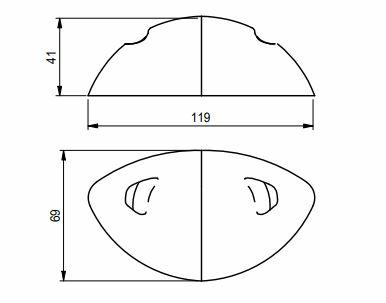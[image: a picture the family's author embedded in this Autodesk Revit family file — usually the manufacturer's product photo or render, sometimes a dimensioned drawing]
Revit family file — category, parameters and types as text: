
# Revit family: R-MBD-483
name_source: partatom
category: Portes
units: mm (PartAtom-declared; Revit-internal decimal feet)

## family parameters
Couper avec des vides une fois chargée = Non
Hôte = Mur
Partagée = Non
Repère de localisation dans la pièce = Oui
Toujours verticalement = Oui

## types (1)
- MBD-483
    1 Vantail = Oui
    2 Vantaux = Non
    A.E.V = non
    Acoustique = non
    Anti-Effraction = non
    Certification = D.A.S. Mode 2 certifié NF
    Code_MAJ = 2303130305MBD483
    Coloris_Chants = BER
    Coloris_Dormant = Hêtre
    Coloris_Face_Cote_Oppose_Ouverture = Prépeint
    Coloris_Face_Cote_Ouverture = Prépeint
    Construction analytique = <Aucun>
    DAS = Oui
    DC Larg Feuillure = 12 mm  [stored 0.0393701 ft]
    DC Pivot Vantail = 60 mm  [stored 0.19685 ft]
    Description = Bloc-porte bois D.A.S. 1 vantail avec pivot linteau motorisé encastré, double action / va-et-vient, EI30, D.A.S. certifié NF, sur huisserie bois sans montant sans fileur
    Définir les propriétés thermiques par = Type schématique
    Ep Profil Pose Tunnel = 118 mm
    Ep Strat Vantail = 1 mm  [stored 0.00328084 ft]
    Ep Vantail = 46 mm  [stored 0.150919 ft]
    Epaisseur_Rainure à brique = 8 mm  [stored 0.0262467 ft]
    Fabricant = MALERBA
    Fiche_Produit = MBD-483
    Fileur = Non
    Hauteur_Tableau = 2125 mm
    Hauteur_Vantaux_Souhaitée = 2040 mm  [stored 6.69291 ft]
    Jeu_1 = 0 mm  [stored 0 ft]
    Jeu_2 = 0 mm  [stored 0 ft]
    Jeu_Côté_Articulation_Vantail = 8 mm  [stored 0.0262467 ft]
    Jeu_Côté_Fermeture_Vantail = 8 mm  [stored 0.0262467 ft]
    Jeu_Haut = 3 mm  [stored 0.00984252 ft]
    Larg Profil = 58 mm  [stored 0.190289 ft]
    Larg Profil Avec Fileur = 20 mm  [stored 0.0656168 ft]
    Larg Profil Trav = 76 mm  [stored 0.249344 ft]
    Largeur = 0 mm  [stored 0 ft]
    Largeur_Vantail_Semi_Fixe_Souhaitée = 930 mm  [stored 3.05118 ft]
    Largeur_Vantail_Service_Souhaitée = 930 mm  [stored 3.05118 ft]
    Mat APD = Caoutchouc noir
    Mat Parclose = BER 2
    Mat Parclose Métal = Peinture Laquée PMT - Blanc Pur - RAL 9010
    Materiaux_Dominant = Bois
    Modèle = Va et vient
    Montant_VV = Non
    Note d'identification = 1V EI30 DAS - LINTEAU MOTORISE - SANS MONTANT SANS FILEUR
    Pivot linteau motorisé = Oui
    Profondeur_Rainure à brique = 5 mm  [stored 0.0164042 ft]
    Reference_Commerciale = 1V/DA LINTEAU OP
    Resistance_Feu = EI30
    Sans_Montants = Oui
    Sens_Feu = Recto / Verso
    Thermique (W/m2.°K) = 0
    URL = https://www.malerba.fr
    X_Axe Pivot = 68 mm  [stored 0.223097 ft]
    X_DC seuil = 9 mm  [stored 0.0295276 ft]
    X_Inv_DC Larg Feuillure_1V Montant = 0 mm  [stored 0 ft]

note: [stored X ft] marks values corroborated as IEEE doubles in the binary element streams (Revit-internal decimal feet)

## geometry (parser evidence)
native form markers: Blend x14
no freeform markers — native parametric forms only
